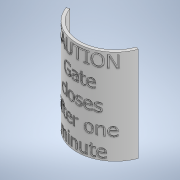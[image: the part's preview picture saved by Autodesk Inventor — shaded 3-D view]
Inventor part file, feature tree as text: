
AUTODESK INVENTOR PART (.ipt)
format: ipt  version: 2021.2 (Build 252289000, 289)  size: 1,514,496 bytes
history: native  units: in
note: dims shown in document units (in); Inventor stores cm internally (conversion verified against a paired STEP export)
features: sketch x2, extrude x1, plane x1, emboss x1
ambient origin geometry x8: Origin, YZ Plane, XZ Plane, XY Plane, X Axis, Y Axis, Z Axis, Center Point
bodies: Solid1 (feature_tree)
feature tree (5):
  extrude  "Extrusion1"  Depth=8.0in TaperAngle=0.0deg
  plane  "Work Plane1"
  emboss  "Emboss1"
  sketch  "Sketch1"  dims[d0=6.0in d2=8.0in d3=0.0in]
  sketch  "Sketch3"  dims[d6=1.0in d7=0.1in d8=0.0in d9=0.25in d10=0.7559in d11=0.7559in]
